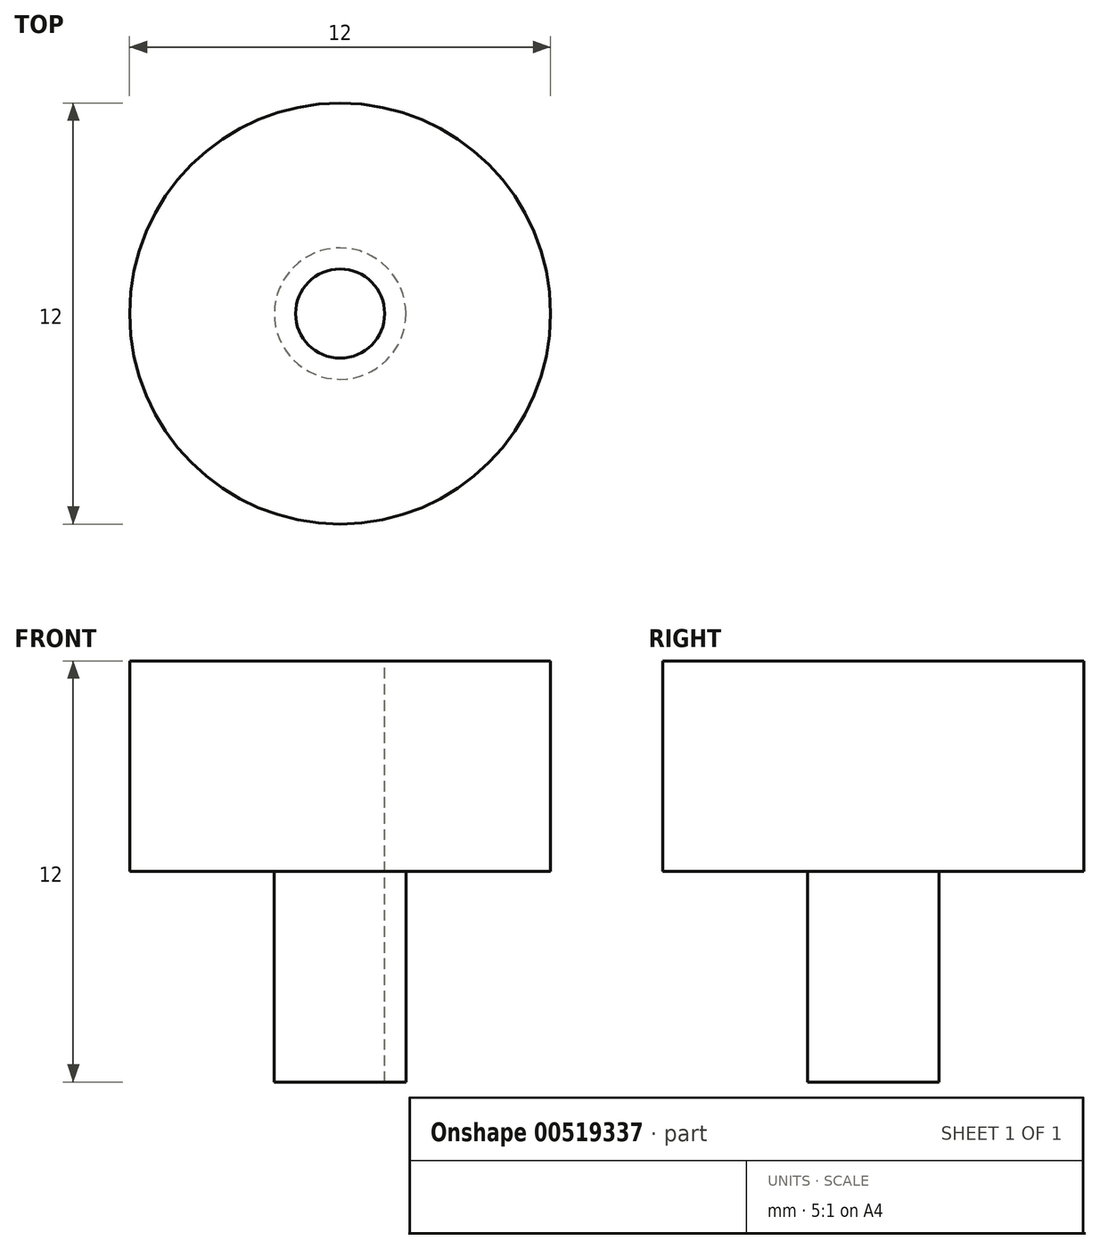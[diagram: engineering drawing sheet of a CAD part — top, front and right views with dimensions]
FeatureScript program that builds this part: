
annotation { "Feature Type Name" : "Feature", "Feature Type Description" : "" }
export const myFeature = defineFeature(function(context is Context, id is Id, definition is map)
    precondition{}
    {
        {
            var Q0;
            Q0=qCreatedBy(makeId("Top.planeOp"),FACE);
            var sketch = newSketch(context, id + "F0", { "sketchPlane" : qUnion([Q0])});
            skCircle(sketch, "E0", {"center": v(-128.23, -56.97) * mm, "radius": 1.87 * mm});
            skSolve(sketch);
        }
        {
            var Q0;
            Q0 = qSketchRegion(id + "F0", true);
            extrude(context, id + "F1", {"entities" : qUnion([Q0]), "depth" : 6 * mm, "offsetDistance" : 25.4 * mm});
        }
        {
            var Q0;
            Q0=makeQuery(id+"F1.opExtrude","CAP_FACE",FACE,{"disambiguationData":[OSD([sQuery(id+"F0.wireOp",EDGE,"E0")])],"isStart":false});
            var sketch = newSketch(context, id + "F2", { "sketchPlane" : qUnion([Q0])});
            skCircle(sketch, "E1", {"center": v(-128.23, -56.97) * mm, "radius": 6 * mm});
            skSolve(sketch);
        }
        {
            var Q0;
            Q0 = qSketchRegion(id + "F2", true);
            extrude(context, id + "F3", {"entities" : qUnion([Q0]), "operationType" : NewBodyOperationType.ADD, "depth" : 6 * mm, "offsetDistance" : 25.4 * mm});
        }
        {
            var Q0;
            Q0=makeQuery(id+"F3.opExtrude","CAP_FACE",FACE,{"disambiguationData":[OSD([sQuery(id+"F2.wireOp",EDGE,"E1")])],"isStart":false});
            var sketch = newSketch(context, id + "F4", { "sketchPlane" : qUnion([Q0])});
            skCircle(sketch, "E2", {"center": v(-128.23, -56.97) * mm, "radius": 1.27 * mm});
            skSolve(sketch);
        }
        {
            var Q0;
            Q0=makeQuery(id+"F4.imprint","IMPRINT",FACE,{"disambiguationData":[TD([[makeQuery(id+"F4.imprint","IMPRINT",EDGE,{"derivedFrom":sQuery(id+"F4.wireOp",EDGE,"E2")}),1.0]])]});
            extrude(context, id + "F5", {"entities" : qUnion([Q0]), "operationType" : NewBodyOperationType.REMOVE, "endBound" : BoundingType.THROUGH_ALL, "oppositeDirection" : true, "depth" : 25.4 * mm, "offsetDistance" : 25.4 * mm});
        }
    });
